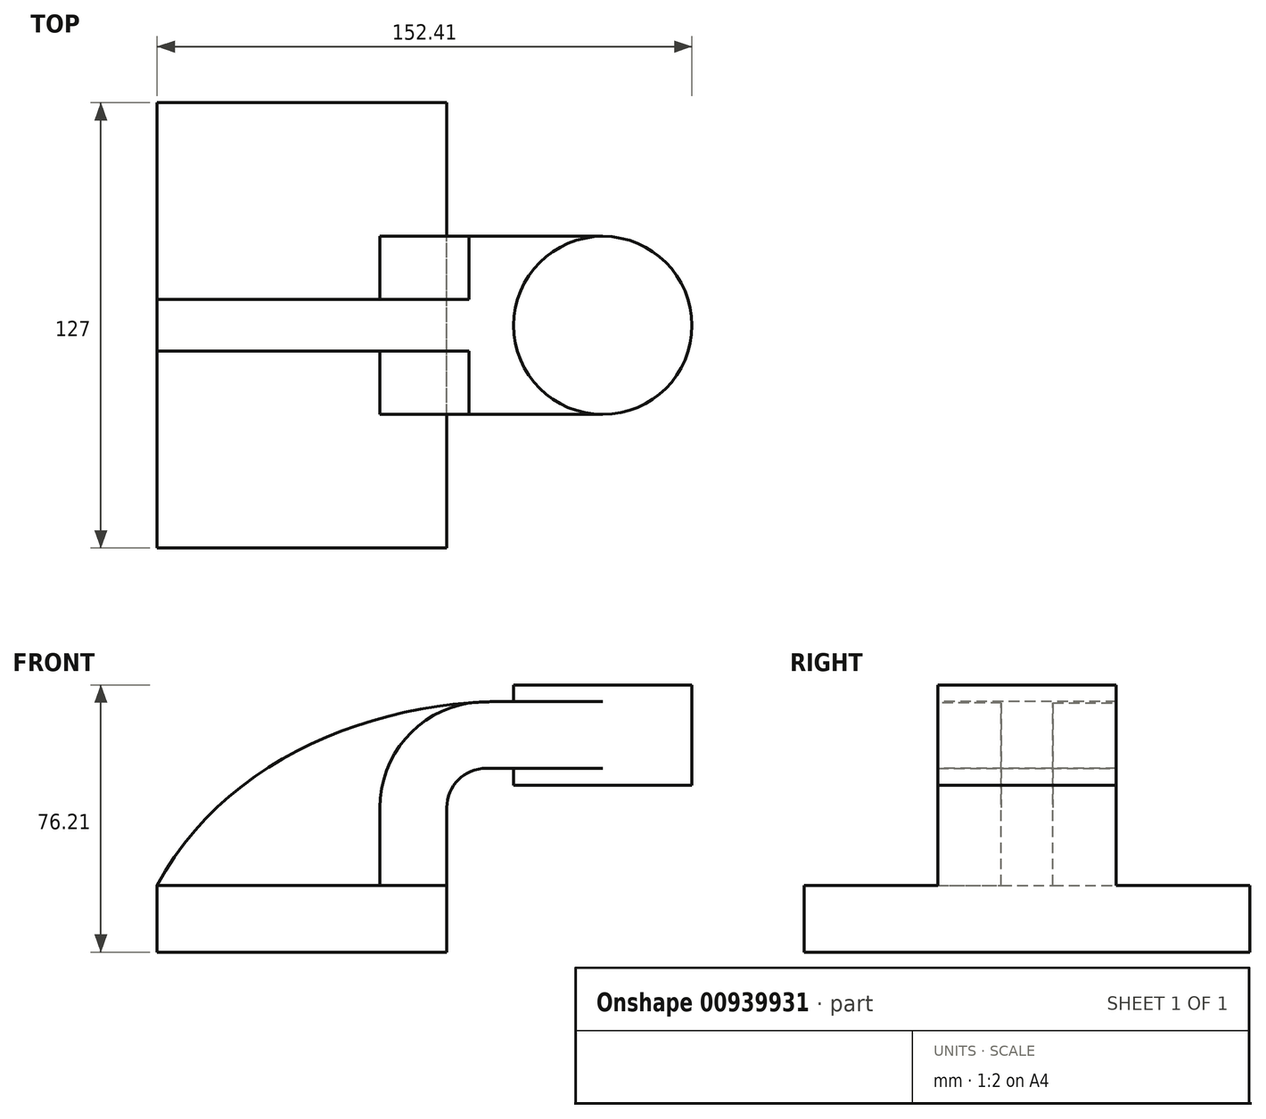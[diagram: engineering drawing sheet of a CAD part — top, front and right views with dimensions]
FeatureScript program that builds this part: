
annotation { "Feature Type Name" : "Feature", "Feature Type Description" : "" }
export const myFeature = defineFeature(function(context is Context, id is Id, definition is map)
    precondition{}
    {
        {
            var Q0;
            Q0=qCreatedBy(makeId("Front.planeOp"),FACE);
            var sketch = newSketch(context, id + "F0", { "sketchPlane" : qUnion([Q0])});
            skLineSegment(sketch, "E0.bottom", {"start": v(-41.28, 9.53) * mm, "end": v(41.28, 9.53) * mm});
            skLineSegment(sketch, "E0.top", {"start": v(-41.28, -9.53) * mm, "end": v(41.28, -9.53) * mm});
            skLineSegment(sketch, "E0.left", {"start": v(-41.28, 9.53) * mm, "end": v(-41.28, -9.53) * mm});
            skLineSegment(sketch, "E0.right", {"start": v(41.28, 9.53) * mm, "end": v(41.28, -9.53) * mm});
            skPoint(sketch, "E0.middle", {"position": v(0, 0) * mm});
            skLineSegment(sketch, "E1", {"start": v(41.28, 9.53) * mm, "end": v(41.28, 31.65) * mm});
            skLineSegment(sketch, "E2.bottom", {"start": v(111.13, 38.1) * mm, "end": v(60.32, 38.1) * mm});
            skLineSegment(sketch, "E2.top", {"start": v(111.12, 66.67) * mm, "end": v(60.32, 66.67) * mm});
            skLineSegment(sketch, "E2.left", {"start": v(111.12, 38.1) * mm, "end": v(111.12, 66.68) * mm});
            skLineSegment(sketch, "E2.right", {"start": v(60.32, 38.1) * mm, "end": v(60.32, 66.67) * mm});
            skPoint(sketch, "E2.middle", {"position": v(85.72, 52.39) * mm});
            skArc(sketch, "E3", {"start": v(41.28, 31.65) * mm, "mid": v(44.56, 39.59) * mm, "end": v(52.5, 42.88) * mm});
            skLineSegment(sketch, "E4", {"start": v(52.5, 42.88) * mm, "end": v(85.72, 42.88) * mm});
            skLineSegment(sketch, "E5.0", {"start": v(52.5, 61.93) * mm, "end": v(85.72, 61.93) * mm});
            skArc(sketch, "E5.1", {"start": v(22.23, 31.65) * mm, "mid": v(31.1, 53.06) * mm, "end": v(52.5, 61.93) * mm});
            skLineSegment(sketch, "E5.2", {"start": v(22.23, 9.53) * mm, "end": v(22.23, 31.65) * mm});
            skFitSpline(sketch, "E6", {"points": [v(-41.28, 9.53) * mm, v(57.42, 61.93) * mm], "startDerivative": vector(57.23, 106.65) * mm, "endDerivative": vector(114.88, 0.41) * mm});
            skLineSegment(sketch, "E7", {"start": v(85.72, 66.67) * mm, "end": v(85.72, 38.1) * mm});
            skSolve(sketch);
        }
        {
            var Q0;
            Q0=makeQuery(id+"F0.imprint","IMPRINT",FACE,{"disambiguationData":[TD([[makeQuery(id+"F0.imprint","IMPRINT",EDGE,{"derivedFrom":sQuery(id+"F0.wireOp",EDGE,"E0.top")}),1.0]])]});
            extrude(context, id + "F1", {"entities" : qUnion([Q0]), "endBound" : BoundingType.SYMMETRIC, "depth" : 127 * mm, "offsetDistance" : 25.4 * mm});
        }
        {
            var Q0;
            {var subQ1=sQuery(id+"F0.wireOp",EDGE,"E1");Q0=makeQuery(id+"F0.imprint","IMPRINT",FACE,{"disambiguationData":[TD([[makeQuery(id+"F0.imprint","IMPRINT",EDGE,{"derivedFrom":subQ1}),1.0]])]});}
            var Q1;
            {var subQ0=sQuery(id+"F0.wireOp",EDGE,"E4");var subQ1=sQuery(id+"F0.wireOp",EDGE,"E2.right");var subQ2=makeQuery(id+"F0.imprint","INTERSECT",VERTEX,{"derivedFrom":[subQ1,subQ0]});Q1=makeQuery(id+"F0.imprint","IMPRINT",FACE,{"disambiguationData":[TD([[makeQuery(id+"F0.imprint","IMPRINT",EDGE,{"disambiguationData":[TD([[subQ2,-1.0]])],"derivedFrom":subQ1}),-1.0]])]});}
            extrude(context, id + "F2", {"entities" : qUnion([Q0, Q1]), "operationType" : NewBodyOperationType.ADD, "endBound" : BoundingType.SYMMETRIC, "depth" : 50.8 * mm, "offsetDistance" : 25.4 * mm});
        }
        {
            var Q0;
            {var subQ3=sQuery(id+"F0.wireOp",EDGE,"E5.2");Q0=makeQuery(id+"F0.imprint","IMPRINT",FACE,{"disambiguationData":[TD([[makeQuery(id+"F0.imprint","IMPRINT",EDGE,{"derivedFrom":subQ3}),1.0]])]});}
            extrude(context, id + "F3", {"entities" : qUnion([Q0]), "operationType" : NewBodyOperationType.ADD, "endBound" : BoundingType.SYMMETRIC, "depth" : 14.73 * mm, "offsetDistance" : 25.4 * mm});
        }
        {
            var Q0;
            {var subQ4=sQuery(id+"F0.wireOp",EDGE,"E2.left");Q0=makeQuery(id+"F0.imprint","IMPRINT",FACE,{"disambiguationData":[TD([[makeQuery(id+"F0.imprint","IMPRINT",EDGE,{"derivedFrom":subQ4}),1.0]])]});}
            var Q1;
            Q1=sQuery(id+"F0.wireOp",EDGE,"E7");
            revolve(context, id + "F4", {"operationType" : NewBodyOperationType.ADD, "surfaceOperationType" : NewSurfaceOperationType.NEW, "entities" : qUnion([Q0]), "axis" : qUnion([Q1]), "revolveType" : RevolveType.FULL});
        }
    });
